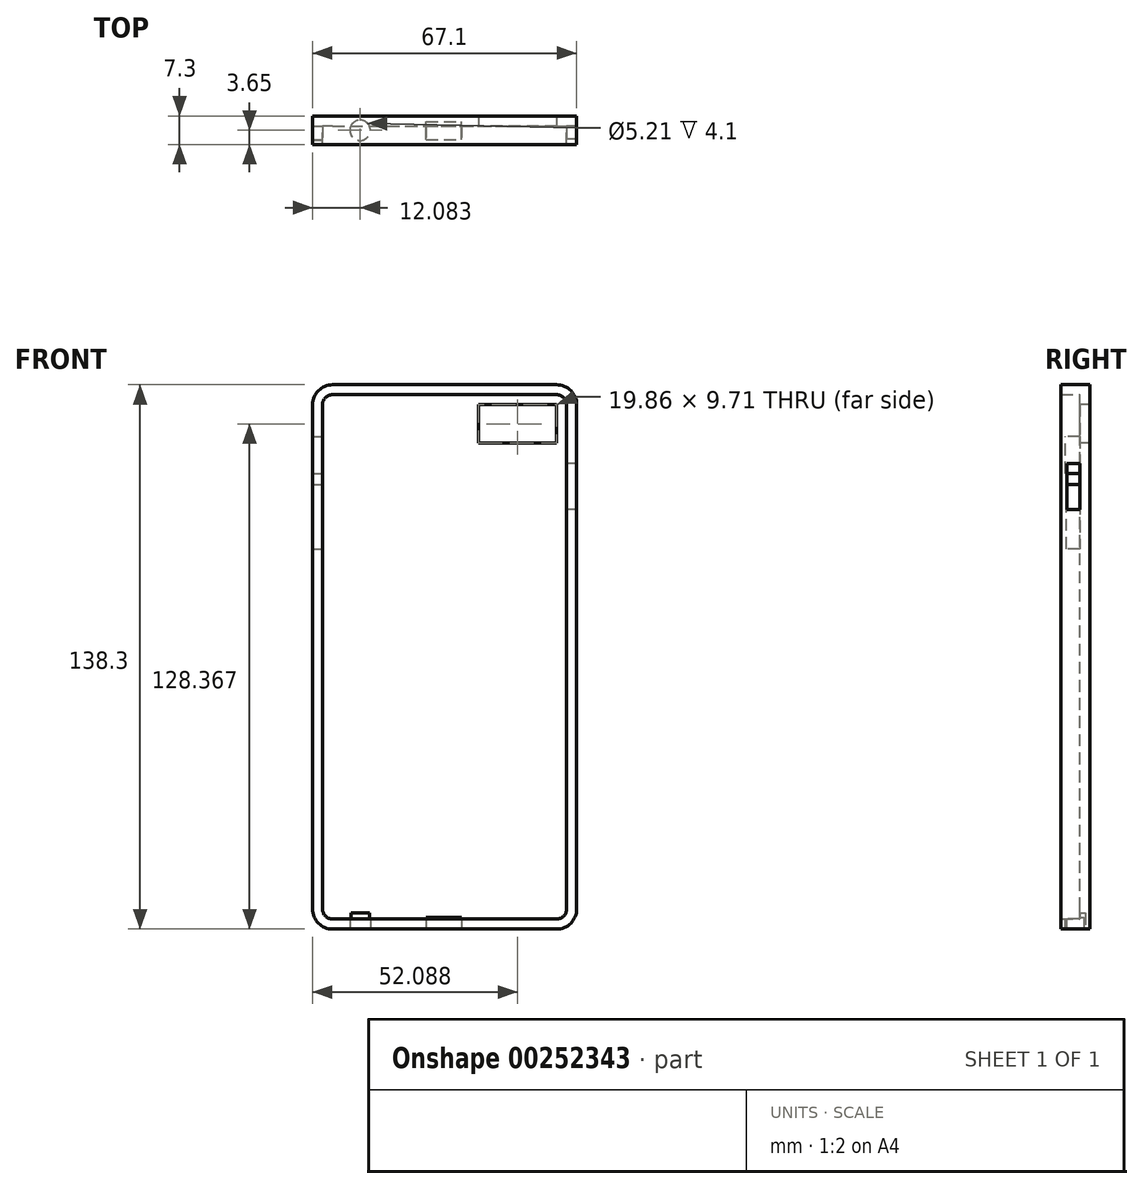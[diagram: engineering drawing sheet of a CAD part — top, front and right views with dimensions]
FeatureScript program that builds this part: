
annotation { "Feature Type Name" : "Feature", "Feature Type Description" : "" }
export const myFeature = defineFeature(function(context is Context, id is Id, definition is map)
    precondition{}
    {
        {
            var Q0;
            Q0=qCreatedBy(makeId("Front.planeOp"),FACE);
            var sketch = newSketch(context, id + "F0", { "sketchPlane" : qUnion([Q0])});
            skLineSegment(sketch, "E0.bottom", {"start": v(-33.55, -69.15) * mm, "end": v(33.55, -69.15) * mm});
            skLineSegment(sketch, "E0.top", {"start": v(-33.55, 69.15) * mm, "end": v(33.55, 69.15) * mm});
            skLineSegment(sketch, "E0.left", {"start": v(-33.55, -69.15) * mm, "end": v(-33.55, 69.15) * mm});
            skLineSegment(sketch, "E0.right", {"start": v(33.55, -69.15) * mm, "end": v(33.55, 69.15) * mm});
            skPoint(sketch, "E0.middle", {"position": v(0, 0) * mm});
            skSolve(sketch);
        }
        {
            var Q0;
            Q0=makeQuery(id+"F0.imprint","IMPRINT",FACE,{"disambiguationData":[TD([[makeQuery(id+"F0.imprint","IMPRINT",EDGE,{"derivedFrom":sQuery(id+"F0.wireOp",EDGE,"E0.bottom")}),1.0]])]});
            extrude(context, id + "F1", {"entities" : qUnion([Q0]), "endBound" : BoundingType.SYMMETRIC, "depth" : 7.3 * mm});
        }
        {
            var Q0;
            Q0=makeQuery(id+"F1.opExtrude","SWEPT_EDGE",EDGE,{"disambiguationData":[OSD([sQuery(id+"F0.wireOp",EDGE,"E0.top"),sQuery(id+"F0.wireOp",EDGE,"E0.left")])]});
            var Q1;
            Q1=makeQuery(id+"F1.opExtrude","SWEPT_EDGE",EDGE,{"disambiguationData":[OSD([sQuery(id+"F0.wireOp",EDGE,"E0.top"),sQuery(id+"F0.wireOp",EDGE,"E0.right")])]});
            var Q2;
            Q2=makeQuery(id+"F1.opExtrude","SWEPT_EDGE",EDGE,{"disambiguationData":[OSD([sQuery(id+"F0.wireOp",EDGE,"E0.bottom"),sQuery(id+"F0.wireOp",EDGE,"E0.right")])]});
            var Q3;
            Q3=makeQuery(id+"F1.opExtrude","SWEPT_EDGE",EDGE,{"disambiguationData":[OSD([sQuery(id+"F0.wireOp",EDGE,"E0.bottom"),sQuery(id+"F0.wireOp",EDGE,"E0.left")])]});
            fillet(context, id + "F2", {"entities" : qUnion([Q0, Q1, Q2, Q3]), "radius" : 5.08 * mm, "tangentPropagation" : true, "allowEdgeOverflow" : false});
        }
        {
            var Q0;
            Q0=makeQuery(id+"F1.opExtrude","CAP_FACE",FACE,{"disambiguationData":[OSD([sQuery(id+"F0.wireOp",EDGE,"E0.bottom"),sQuery(id+"F0.wireOp",EDGE,"E0.top"),sQuery(id+"F0.wireOp",EDGE,"E0.left"),sQuery(id+"F0.wireOp",EDGE,"E0.right")])],"isStart":false});
            shell(context, id + "F3", {"entities" : qUnion([Q0]), "thickness" : 2.54 * mm});
        }
        {
            var Q0;
            Q0=makeQuery(id+"F1.opExtrude","CAP_FACE",FACE,{"disambiguationData":[OSD([sQuery(id+"F0.wireOp",EDGE,"E0.bottom"),sQuery(id+"F0.wireOp",EDGE,"E0.top"),sQuery(id+"F0.wireOp",EDGE,"E0.left"),sQuery(id+"F0.wireOp",EDGE,"E0.right")])],"isStart":true});
            var sketch = newSketch(context, id + "F4", { "sketchPlane" : qUnion([Q0])});
            skLineSegment(sketch, "E1.bottom", {"start": v(-28.47, 64.07) * mm, "end": v(-8.6, 64.07) * mm});
            skLineSegment(sketch, "E1.top", {"start": v(-28.47, 54.36) * mm, "end": v(-8.6, 54.36) * mm});
            skLineSegment(sketch, "E1.left", {"start": v(-28.47, 64.07) * mm, "end": v(-28.47, 54.36) * mm});
            skLineSegment(sketch, "E1.right", {"start": v(-8.6, 64.07) * mm, "end": v(-8.6, 54.36) * mm});
            skSolve(sketch);
        }
        {
            var Q0;
            Q0=makeQuery(id+"F4.imprint","IMPRINT",FACE,{"disambiguationData":[TD([[makeQuery(id+"F4.imprint","IMPRINT",EDGE,{"derivedFrom":sQuery(id+"F4.wireOp",EDGE,"E1.bottom")}),-1.0]])]});
            extrude(context, id + "F5", {"entities" : qUnion([Q0]), "operationType" : NewBodyOperationType.REMOVE, "endBound" : BoundingType.SYMMETRIC, "depth" : 25 * mm});
        }
        {
            var Q0;
            Q0=makeQuery(id+"F1.opExtrude","SWEPT_FACE",FACE,{"disambiguationData":[OSD([sQuery(id+"F0.wireOp",EDGE,"E0.bottom")])]});
            var sketch = newSketch(context, id + "F6", { "sketchPlane" : qUnion([Q0])});
            skLineSegment(sketch, "E2.bottom", {"start": v(-4.7, 2.31) * mm, "end": v(4.28, 2.31) * mm});
            skLineSegment(sketch, "E2.top", {"start": v(-4.7, -2.17) * mm, "end": v(4.28, -2.17) * mm});
            skLineSegment(sketch, "E2.left", {"start": v(-4.7, 2.31) * mm, "end": v(-4.7, -2.17) * mm});
            skLineSegment(sketch, "E2.right", {"start": v(4.28, 2.31) * mm, "end": v(4.28, -2.17) * mm});
            skSolve(sketch);
        }
        {
            var Q0;
            Q0=makeQuery(id+"F6.imprint","IMPRINT",FACE,{"disambiguationData":[TD([[makeQuery(id+"F6.imprint","IMPRINT",EDGE,{"derivedFrom":sQuery(id+"F6.wireOp",EDGE,"E2.bottom")}),-1.0]])]});
            extrude(context, id + "F7", {"entities" : qUnion([Q0]), "operationType" : NewBodyOperationType.REMOVE, "oppositeDirection" : true, "depth" : 3 * mm});
        }
        {
            var Q0;
            Q0=makeQuery(id+"F3.opShell","OFFSET_FACE",FACE,{"disambiguationData":[OSD([sQuery(id+"F0.wireOp",EDGE,"E0.left")])]});
            var sketch = newSketch(context, id + "F8", { "sketchPlane" : qUnion([Q0])});
            skLineSegment(sketch, "E3.bottom", {"start": v(-2.53, 56) * mm, "end": v(1.1, 56) * mm});
            skLineSegment(sketch, "E3.top", {"start": v(-2.53, 46.6) * mm, "end": v(1.1, 46.6) * mm});
            skLineSegment(sketch, "E3.left", {"start": v(-2.53, 56) * mm, "end": v(-2.53, 46.6) * mm});
            skLineSegment(sketch, "E3.right", {"start": v(1.1, 56) * mm, "end": v(1.1, 46.6) * mm});
            skLineSegment(sketch, "E4.bottom", {"start": v(-2.3, 43.8) * mm, "end": v(1.1, 43.8) * mm});
            skLineSegment(sketch, "E4.top", {"start": v(-2.3, 27.47) * mm, "end": v(1.1, 27.47) * mm});
            skLineSegment(sketch, "E4.left", {"start": v(-2.3, 43.8) * mm, "end": v(-2.3, 27.47) * mm});
            skLineSegment(sketch, "E4.right", {"start": v(1.1, 43.8) * mm, "end": v(1.1, 27.47) * mm});
            skSolve(sketch);
        }
        {
            var Q0;
            Q0=makeQuery(id+"F8.imprint","IMPRINT",FACE,{"disambiguationData":[TD([[makeQuery(id+"F8.imprint","IMPRINT",EDGE,{"derivedFrom":sQuery(id+"F8.wireOp",EDGE,"E3.bottom")}),-1.0]])]});
            var Q1;
            Q1=makeQuery(id+"F8.imprint","IMPRINT",FACE,{"disambiguationData":[TD([[makeQuery(id+"F8.imprint","IMPRINT",EDGE,{"derivedFrom":sQuery(id+"F8.wireOp",EDGE,"E4.bottom")}),-1.0]])]});
            extrude(context, id + "F9", {"entities" : qUnion([Q0, Q1]), "operationType" : NewBodyOperationType.REMOVE, "endBound" : BoundingType.SYMMETRIC, "oppositeDirection" : true, "depth" : 16.6 * mm});
        }
        {
            var Q0;
            Q0=makeQuery(id+"F3.opShell","OFFSET_FACE",FACE,{"disambiguationData":[OSD([sQuery(id+"F0.wireOp",EDGE,"E0.right")])]});
            var sketch = newSketch(context, id + "F10", { "sketchPlane" : qUnion([Q0])});
            skLineSegment(sketch, "E5.bottom", {"start": v(-1.1, 49.08) * mm, "end": v(2.2, 49.08) * mm});
            skLineSegment(sketch, "E5.top", {"start": v(-1.1, 37.47) * mm, "end": v(2.2, 37.47) * mm});
            skLineSegment(sketch, "E5.left", {"start": v(-1.1, 49.08) * mm, "end": v(-1.1, 37.47) * mm});
            skLineSegment(sketch, "E5.right", {"start": v(2.2, 49.08) * mm, "end": v(2.2, 37.47) * mm});
            skSolve(sketch);
        }
        {
            var Q0;
            Q0=makeQuery(id+"F10.imprint","IMPRINT",FACE,{"disambiguationData":[TD([[makeQuery(id+"F10.imprint","IMPRINT",EDGE,{"derivedFrom":sQuery(id+"F10.wireOp",EDGE,"E5.bottom")}),-1.0]])]});
            extrude(context, id + "F11", {"entities" : qUnion([Q0]), "operationType" : NewBodyOperationType.REMOVE, "endBound" : BoundingType.SYMMETRIC, "oppositeDirection" : true, "depth" : 9.4 * mm});
        }
        {
            var Q0;
            Q0=makeQuery(id+"F1.opExtrude","SWEPT_FACE",FACE,{"disambiguationData":[OSD([sQuery(id+"F0.wireOp",EDGE,"E0.bottom")])]});
            var sketch = newSketch(context, id + "F12", { "sketchPlane" : qUnion([Q0])});
            skPoint(sketch, "E6", {"position": v(8.45, 0) * mm});
            skPoint(sketch, "E7", {"position": v(12.26, 0) * mm});
            skPoint(sketch, "E8", {"position": v(15.8, 0) * mm});
            skPoint(sketch, "E9", {"position": v(19.57, 0) * mm});
            skPoint(sketch, "E10", {"position": v(23.55, 0) * mm});
            skPoint(sketch, "E11", {"position": v(26.94, 0) * mm});
            skSolve(sketch);
        }
        {
            var Q0;
            {var subQ0=sQuery(id+"F0.wireOp",EDGE,"E0.bottom");Q0=makeQuery(id+"F12.imprint","IMPRINT",FACE,{"disambiguationData":[TD([[makeQuery(id+"F12.imprint","IMPRINT",EDGE,{"derivedFrom":makeQuery(id+"F1.opExtrude","CAP_EDGE",EDGE,{"disambiguationData":[OSD([subQ0])],"isStart":true})}),1.0]])]});}
            var sketch = newSketch(context, id + "F13", { "sketchPlane" : qUnion([Q0])});
            skCircle(sketch, "E12", {"center": v(-21.47, 0) * mm, "radius": 2.6 * mm});
            skCircle(sketch, "E13", {"center": v(-16.83, 0) * mm, "radius": 1.17 * mm});
            skSolve(sketch);
        }
        {
            var Q0;
            Q0=makeQuery(id+"F13.imprint","IMPRINT",FACE,{"disambiguationData":[TD([[makeQuery(id+"F13.imprint","IMPRINT",EDGE,{"derivedFrom":sQuery(id+"F13.wireOp",EDGE,"E12")}),1.0]])]});
            extrude(context, id + "F14", {"entities" : qUnion([Q0]), "operationType" : NewBodyOperationType.REMOVE, "endBound" : BoundingType.SYMMETRIC, "oppositeDirection" : true, "depth" : 8.2 * mm});
        }
    });
